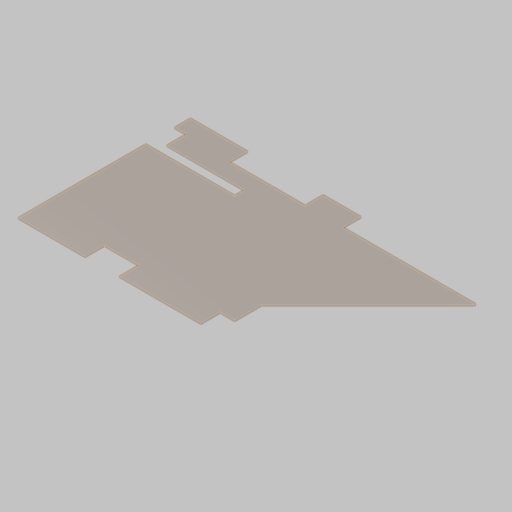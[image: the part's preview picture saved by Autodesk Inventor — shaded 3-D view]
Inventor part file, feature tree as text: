
AUTODESK INVENTOR PART (.ipt)
format: ipt  version: 2023.5 (Build 275446000, 446)  size: 274,432 bytes
history: native  units: in
note: dims shown in document units (in); Inventor stores cm internally (conversion verified against a paired STEP export)
features: sketch x5, other x3, projected_geometry x3, sheet_metal_op x1, extrude x1
ambient origin geometry x8: Origin, YZ Plane, XZ Plane, XY Plane, X Axis, Y Axis, Z Axis, Center Point
bodies: Solid1 (feature_tree)
feature tree (13):
  sheet_metal_op  "Face1"
  sketch  "Sketch3"  dims[d2=0.12in]
  extrude  "Extrusion1"  Depth=28.0in
  sketch  "Sketch1"  dims[d0=18.5in d1=28.0in]
  other  "Plate1"
  sketch  "Sketch4"  dims[d3=8.25in]
  projected_geometry  "Projected Loop1"
  sketch  "Sketch5"  dims[d4=10.0in]
  sketch  "Sketch6"  dims[d5=45.0deg d6=2.4in d9=2.75in d10=0.12in d11=0.0in d12=45.0deg d13=8.25in d14=9.0in d15=2.75in d16=2.4in d17=6.75in d18=4.5in d19=0.25in d21=4.0in d22=1.0in d23=0.1in d26=5.7in d31=0.5in d32=4.5in d33=6.75in d34=0.25in d35=4.0in d36=1.0in d37=0.1in d38=3.0in d39=1.4in d40=1.7in d41=0.1in d42=1.0in d43=0.75in d44=1.0in d45=0.75in d46=0.75in d47=1.0in d48=0.75in d49=1.0in d50=0.12in d51=0.0in d52=1.75in d53=1.0in d54=3.5in d55=1.75in d56=1.0in d57=3.5in d58=1.0in d59=0.125in d60=3.0in d61=2.0in d62=11.0in d63=1.0in d64=0.0in d65=0.125in d66=0.125in d67=0.125in d68=0.125in d69=0.125in d70=0.125in d71=0.125in d72=0.125in d73=0.0625in]
  other  "Cut1"
  other  "Cut2"
  projected_geometry  "Project Cut Edges1"
  projected_geometry  "Project Cut Edges2"
